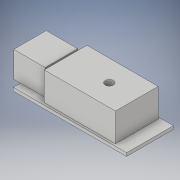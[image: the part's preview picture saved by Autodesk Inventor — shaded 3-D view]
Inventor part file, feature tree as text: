
AUTODESK INVENTOR PART (.ipt)
format: ipt  version: 2018 (Build 220112000, 112)  size: 133,120 bytes
history: native  units: in
note: dims shown in document units (in); Inventor stores cm internally (conversion verified against a paired STEP export)
features: extrude x4, sketch x4
ambient origin geometry x8: Origin, YZ Plane, XZ Plane, XY Plane, X Axis, Y Axis, Z Axis, Center Point
bodies: Solid1 (feature_tree)
feature tree (8):
  extrude  "Extrusion1"  Depth=2.1949in
  extrude  "Extrusion2"  Depth=0.6102in
  extrude  "Extrusion3"  Depth=0.128in
  extrude  "Extrusion4"  Depth=0.502in TaperAngle=0.0deg
  sketch  "Sketch1"  dims[d0=0.9055in d1=2.1949in]
  sketch  "Sketch2"  dims[d2=0.063in d3=0.0in d5=0.6102in]
  sketch  "Sketch3"  dims[d6=0.6299in d7=0.128in]
  sketch  "Sketch4"  dims[d9=0.0in d10=0.502in d11=0.0in d12=0.2559in d13=0.8268in d14=1.378in d15=0.5512in d16=0.0in d17=0.7874in d18=0.1575in d19=1.0in d20=0.0in]
